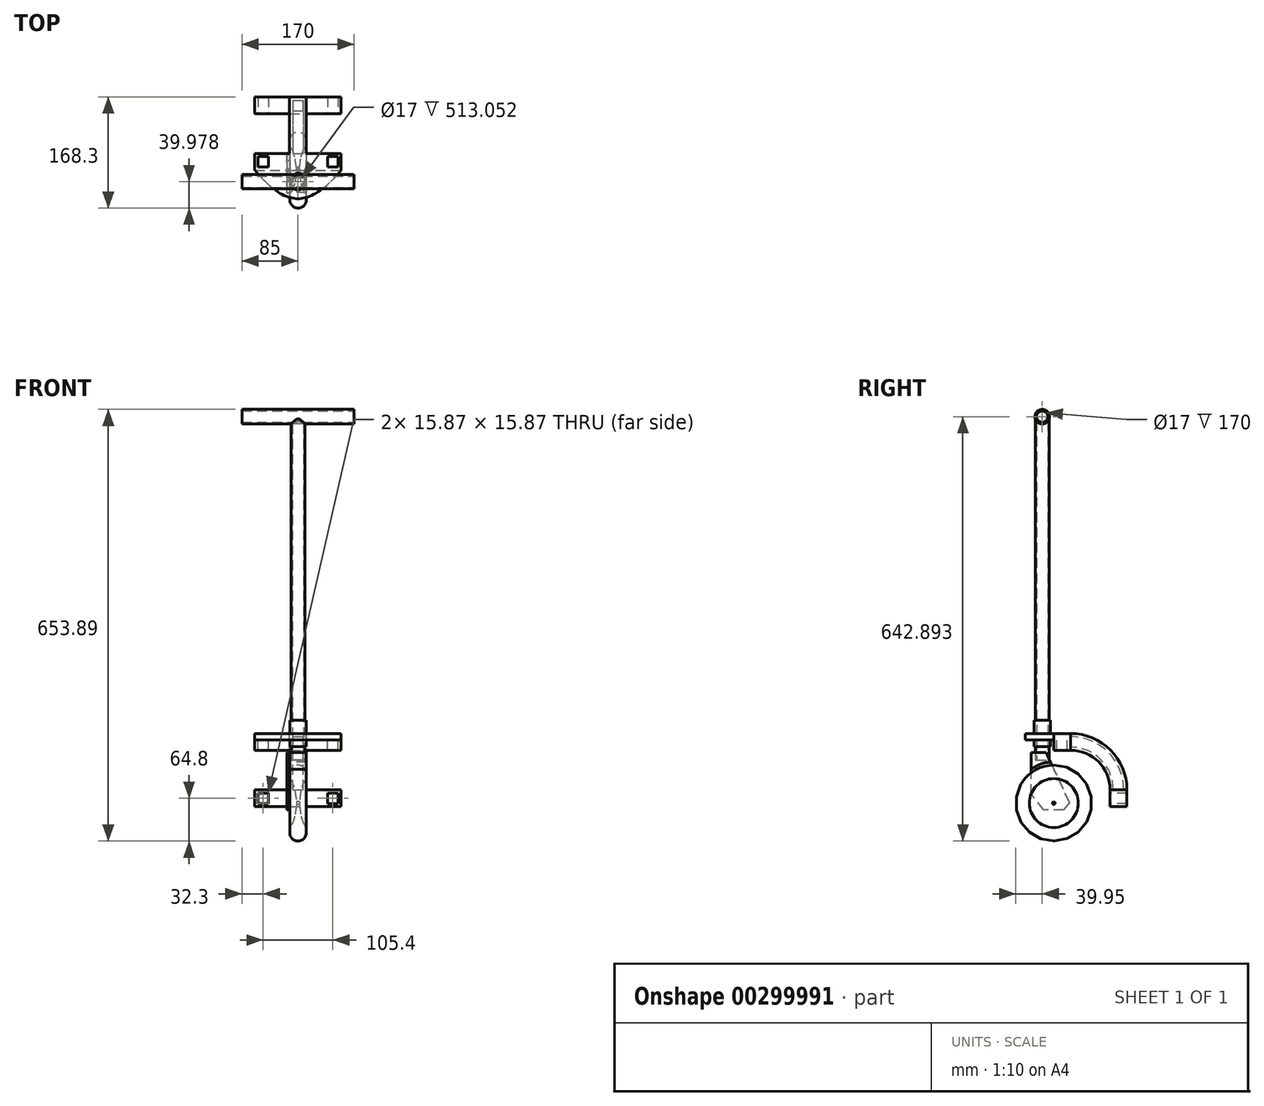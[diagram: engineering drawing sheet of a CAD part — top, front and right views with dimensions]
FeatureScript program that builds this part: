
annotation { "Feature Type Name" : "Feature", "Feature Type Description" : "" }
export const myFeature = defineFeature(function(context is Context, id is Id, definition is map)
    precondition{}
    {
        {
            var Q0;
            Q0=qCreatedBy(makeId("Top.planeOp"),FACE);
            var sketch = newSketch(context, id + "F0", { "sketchPlane" : qUnion([Q0])});
            skLineSegment(sketch, "E0.bottom", {"start": v(-12.7, 25.4) * mm, "end": v(12.7, 25.4) * mm});
            skLineSegment(sketch, "E0.top", {"start": v(-12.7, 0) * mm, "end": v(12.7, 0) * mm});
            skLineSegment(sketch, "E0.left", {"start": v(-12.7, 25.4) * mm, "end": v(-12.7, 0) * mm});
            skLineSegment(sketch, "E0.right", {"start": v(12.7, 25.4) * mm, "end": v(12.7, 0) * mm});
            skLineSegment(sketch, "E1.bottom", {"start": v(-7.94, 20.63) * mm, "end": v(7.94, 20.63) * mm});
            skLineSegment(sketch, "E1.top", {"start": v(-7.94, 4.76) * mm, "end": v(7.94, 4.76) * mm});
            skLineSegment(sketch, "E1.left", {"start": v(-7.94, 20.63) * mm, "end": v(-7.94, 4.76) * mm});
            skLineSegment(sketch, "E1.right", {"start": v(7.94, 20.63) * mm, "end": v(7.94, 4.76) * mm});
            skSolve(sketch);
        }
        {
            var Q0;
            Q0=qCreatedBy(makeId("Right.planeOp"),FACE);
            var sketch = newSketch(context, id + "F1", { "sketchPlane" : qUnion([Q0])});
            skArc(sketch, "E2", {"start": v(0, 0) * mm, "mid": v(-17.57, 42.43) * mm, "end": v(-60, 60) * mm});
            skSolve(sketch);
        }
        {
            var Q0;
            Q0 = qSketchRegion(id + "F0", true);
            var Q1;
            Q1=sQuery(id+"F1.wireOp",EDGE,"E2");
            sweep(context, id + "F2", {"profiles" : qUnion([Q0]), "path" : qUnion([Q1])});
        }
        {
            var Q0;
            Q0=makeQuery(id+"F2.opSweep","CAP_FACE",FACE,{"disambiguationData":[OSD([sQuery(id+"F0.wireOp",EDGE,"E0.bottom"),sQuery(id+"F0.wireOp",EDGE,"E0.top"),sQuery(id+"F0.wireOp",EDGE,"E0.left"),sQuery(id+"F0.wireOp",EDGE,"E0.right"),sQuery(id+"F0.wireOp",EDGE,"E1.bottom"),sQuery(id+"F0.wireOp",EDGE,"E1.top"),sQuery(id+"F0.wireOp",EDGE,"E1.left"),sQuery(id+"F0.wireOp",EDGE,"E1.right"),sQuery(id+"F1.wireOp",VERTEX,"E2.end")])],"isStart":false});
            var sketch = newSketch(context, id + "F3", { "sketchPlane" : qUnion([Q0])});
            skLineSegment(sketch, "E3.bottom", {"start": v(-12.7, 85.4) * mm, "end": v(12.7, 85.4) * mm});
            skLineSegment(sketch, "E3.top", {"start": v(-12.7, 60) * mm, "end": v(12.7, 60) * mm});
            skLineSegment(sketch, "E3.left", {"start": v(-12.7, 85.4) * mm, "end": v(-12.7, 60) * mm});
            skLineSegment(sketch, "E3.right", {"start": v(12.7, 85.4) * mm, "end": v(12.7, 60) * mm});
            skLineSegment(sketch, "E4.bottom", {"start": v(-7.94, 80.63) * mm, "end": v(7.94, 80.63) * mm});
            skLineSegment(sketch, "E4.top", {"start": v(-7.94, 64.76) * mm, "end": v(7.94, 64.76) * mm});
            skLineSegment(sketch, "E4.left", {"start": v(-7.94, 80.63) * mm, "end": v(-7.94, 64.76) * mm});
            skLineSegment(sketch, "E4.right", {"start": v(7.94, 80.63) * mm, "end": v(7.94, 64.76) * mm});
            skSolve(sketch);
        }
        {
            var Q0;
            Q0 = qSketchRegion(id + "F3", true);
            extrude(context, id + "F4", {"entities" : qUnion([Q0]), "operationType" : NewBodyOperationType.ADD, "depth" : 25.4 * mm, "offsetDistance" : 25 * mm});
        }
        {
            var Q0;
            Q0=makeQuery(id+"F2.opSweep","CAP_FACE",FACE,{"disambiguationData":[OSD([sQuery(id+"F0.wireOp",EDGE,"E0.bottom"),sQuery(id+"F0.wireOp",EDGE,"E0.top"),sQuery(id+"F0.wireOp",EDGE,"E0.left"),sQuery(id+"F0.wireOp",EDGE,"E0.right"),sQuery(id+"F0.wireOp",EDGE,"E1.bottom"),sQuery(id+"F0.wireOp",EDGE,"E1.top"),sQuery(id+"F0.wireOp",EDGE,"E1.left"),sQuery(id+"F0.wireOp",EDGE,"E1.right"),sQuery(id+"F1.wireOp",VERTEX,"E2.start")])],"isStart":true});
            var sketch = newSketch(context, id + "F5", { "sketchPlane" : qUnion([Q0])});
            skLineSegment(sketch, "E5.bottom", {"start": v(-12.7, 0) * mm, "end": v(12.7, 0) * mm});
            skLineSegment(sketch, "E5.top", {"start": v(-12.7, -25.4) * mm, "end": v(12.7, -25.4) * mm});
            skLineSegment(sketch, "E5.left", {"start": v(-12.7, 0) * mm, "end": v(-12.7, -25.4) * mm});
            skLineSegment(sketch, "E5.right", {"start": v(12.7, 0) * mm, "end": v(12.7, -25.4) * mm});
            skLineSegment(sketch, "E6.bottom", {"start": v(-7.94, -4.76) * mm, "end": v(7.94, -4.76) * mm});
            skLineSegment(sketch, "E6.top", {"start": v(-7.94, -20.63) * mm, "end": v(7.94, -20.63) * mm});
            skLineSegment(sketch, "E6.left", {"start": v(-7.94, -4.76) * mm, "end": v(-7.94, -20.63) * mm});
            skLineSegment(sketch, "E6.right", {"start": v(7.94, -4.76) * mm, "end": v(7.94, -20.63) * mm});
            skSolve(sketch);
        }
        {
            var Q0;
            Q0=makeQuery(id+"F5.imprint","IMPRINT",FACE,{"disambiguationData":[TD([[makeQuery(id+"F5.imprint","IMPRINT",EDGE,{"derivedFrom":sQuery(id+"F5.wireOp",EDGE,"E5.bottom")}),-1.0]])]});
            extrude(context, id + "F6", {"entities" : qUnion([Q0]), "operationType" : NewBodyOperationType.ADD, "depth" : 25.4 * mm, "offsetDistance" : 25 * mm});
        }
        {
            var Q0;
            Q0=qCreatedBy(makeId("Right.planeOp"),FACE);
            var sketch = newSketch(context, id + "F7", { "sketchPlane" : qUnion([Q0])});
            skLineSegment(sketch, "E7.bottom", {"start": v(0, 0) * mm, "end": v(25.4, 0) * mm});
            skLineSegment(sketch, "E7.top", {"start": v(0, -25.4) * mm, "end": v(25.4, -25.4) * mm});
            skLineSegment(sketch, "E7.left", {"start": v(0, 0) * mm, "end": v(0, -25.4) * mm});
            skLineSegment(sketch, "E7.right", {"start": v(25.4, 0) * mm, "end": v(25.4, -25.4) * mm});
            skLineSegment(sketch, "E8.bottom", {"start": v(-85.4, 60) * mm, "end": v(-60, 60) * mm});
            skLineSegment(sketch, "E8.top", {"start": v(-85.4, 85.4) * mm, "end": v(-60, 85.4) * mm});
            skLineSegment(sketch, "E8.left", {"start": v(-85.4, 60) * mm, "end": v(-85.4, 85.4) * mm});
            skLineSegment(sketch, "E8.right", {"start": v(-60, 60) * mm, "end": v(-60, 85.4) * mm});
            skSolve(sketch);
        }
        {
            var Q0;
            Q0=makeQuery(id+"F7.imprint","IMPRINT",FACE,{"disambiguationData":[TD([[makeQuery(id+"F7.imprint","IMPRINT",EDGE,{"derivedFrom":sQuery(id+"F7.wireOp",EDGE,"E7.bottom")}),-1.0]])]});
            var Q1;
            Q1=makeQuery(id+"F7.imprint","IMPRINT",FACE,{"disambiguationData":[TD([[makeQuery(id+"F7.imprint","IMPRINT",EDGE,{"derivedFrom":sQuery(id+"F7.wireOp",EDGE,"E8.bottom")}),1.0]])]});
            extrude(context, id + "F8", {"entities" : qUnion([Q0, Q1]), "operationType" : NewBodyOperationType.ADD, "endBound" : BoundingType.SYMMETRIC, "depth" : 80 * mm});
        }
        {
            var Q0;
            Q0=makeQuery(id+"F6.opExtrude","SWEPT_FACE",FACE,{"disambiguationData":[OSD([sQuery(id+"F5.wireOp",EDGE,"E5.bottom")])]});
            var sketch = newSketch(context, id + "F9", { "sketchPlane" : qUnion([Q0])});
            skLineSegment(sketch, "E9.bottom", {"start": v(40, 0) * mm, "end": v(65.4, 0) * mm});
            skLineSegment(sketch, "E9.top", {"start": v(40, -25.4) * mm, "end": v(65.4, -25.4) * mm});
            skLineSegment(sketch, "E9.left", {"start": v(40, 0) * mm, "end": v(40, -25.4) * mm});
            skLineSegment(sketch, "E9.right", {"start": v(65.4, 0) * mm, "end": v(65.4, -25.4) * mm});
            skLineSegment(sketch, "E10.bottom", {"start": v(-40, 0) * mm, "end": v(-65.4, 0) * mm});
            skLineSegment(sketch, "E10.top", {"start": v(-40, -25.4) * mm, "end": v(-65.4, -25.4) * mm});
            skLineSegment(sketch, "E10.left", {"start": v(-40, 0) * mm, "end": v(-40, -25.4) * mm});
            skLineSegment(sketch, "E10.right", {"start": v(-65.4, 0) * mm, "end": v(-65.4, -25.4) * mm});
            skLineSegment(sketch, "E11.bottom", {"start": v(-60.64, -4.76) * mm, "end": v(-44.76, -4.76) * mm});
            skLineSegment(sketch, "E11.top", {"start": v(-60.64, -20.64) * mm, "end": v(-44.76, -20.64) * mm});
            skLineSegment(sketch, "E11.left", {"start": v(-60.64, -4.76) * mm, "end": v(-60.64, -20.64) * mm});
            skLineSegment(sketch, "E11.right", {"start": v(-44.76, -4.76) * mm, "end": v(-44.76, -20.64) * mm});
            skLineSegment(sketch, "E12.bottom", {"start": v(44.76, -4.76) * mm, "end": v(60.64, -4.76) * mm});
            skLineSegment(sketch, "E12.top", {"start": v(44.76, -20.64) * mm, "end": v(60.64, -20.64) * mm});
            skLineSegment(sketch, "E12.left", {"start": v(44.76, -4.76) * mm, "end": v(44.76, -20.64) * mm});
            skLineSegment(sketch, "E12.right", {"start": v(60.64, -4.76) * mm, "end": v(60.64, -20.64) * mm});
            skSolve(sketch);
        }
        {
            var Q0;
            Q0 = qSketchRegion(id + "F9", true);
            extrude(context, id + "F10", {"entities" : qUnion([Q0]), "operationType" : NewBodyOperationType.ADD, "oppositeDirection" : true, "depth" : 25.4 * mm, "offsetDistance" : 25 * mm});
        }
        {
            var Q0;
            Q0=makeQuery(id+"F8.boolean.opBoolean","MERGE",FACE,{"derivedFrom":[makeQuery(id+"F4.opExtrude","SWEPT_FACE",FACE,{"disambiguationData":[OSD([sQuery(id+"F3.wireOp",EDGE,"E3.bottom")])]}),makeQuery(id+"F8.opExtrude","SWEPT_FACE",FACE,{"disambiguationData":[OSD([sQuery(id+"F7.wireOp",EDGE,"E8.top")])]})]});
            var sketch = newSketch(context, id + "F11", { "sketchPlane" : qUnion([Q0])});
            skLineSegment(sketch, "E13.bottom", {"start": v(-65.4, -60) * mm, "end": v(-40, -60) * mm});
            skLineSegment(sketch, "E13.top", {"start": v(-65.4, -85.4) * mm, "end": v(-40, -85.4) * mm});
            skLineSegment(sketch, "E13.left", {"start": v(-65.4, -60) * mm, "end": v(-65.4, -85.4) * mm});
            skLineSegment(sketch, "E13.right", {"start": v(-40, -60) * mm, "end": v(-40, -85.4) * mm});
            skLineSegment(sketch, "E14.bottom", {"start": v(40, -60) * mm, "end": v(65.4, -60) * mm});
            skLineSegment(sketch, "E14.top", {"start": v(40, -85.4) * mm, "end": v(65.4, -85.4) * mm});
            skLineSegment(sketch, "E14.left", {"start": v(40, -60) * mm, "end": v(40, -85.4) * mm});
            skLineSegment(sketch, "E14.right", {"start": v(65.4, -60) * mm, "end": v(65.4, -85.4) * mm});
            skLineSegment(sketch, "E15.bottom", {"start": v(-60.64, -64.76) * mm, "end": v(-44.76, -64.76) * mm});
            skLineSegment(sketch, "E15.top", {"start": v(-60.64, -80.64) * mm, "end": v(-44.76, -80.64) * mm});
            skLineSegment(sketch, "E15.left", {"start": v(-60.64, -64.76) * mm, "end": v(-60.64, -80.64) * mm});
            skLineSegment(sketch, "E15.right", {"start": v(-44.76, -64.76) * mm, "end": v(-44.76, -80.64) * mm});
            skLineSegment(sketch, "E16.bottom", {"start": v(44.76, -64.76) * mm, "end": v(60.64, -64.76) * mm});
            skLineSegment(sketch, "E16.top", {"start": v(44.76, -80.64) * mm, "end": v(60.64, -80.64) * mm});
            skLineSegment(sketch, "E16.left", {"start": v(44.76, -64.76) * mm, "end": v(44.76, -80.64) * mm});
            skLineSegment(sketch, "E16.right", {"start": v(60.64, -64.76) * mm, "end": v(60.64, -80.64) * mm});
            skSolve(sketch);
        }
        {
            var Q0;
            Q0 = qSketchRegion(id + "F11", true);
            extrude(context, id + "F12", {"entities" : qUnion([Q0]), "operationType" : NewBodyOperationType.ADD, "oppositeDirection" : true, "depth" : 25.4 * mm, "offsetDistance" : 25 * mm});
        }
        {
            var Q0;
            Q0=makeQuery(id+"F12.boolean.opBoolean","MERGE",FACE,{"derivedFrom":[makeQuery(id+"F8.boolean.opBoolean","MERGE",FACE,{"derivedFrom":[makeQuery(id+"F4.opExtrude","SWEPT_FACE",FACE,{"disambiguationData":[OSD([sQuery(id+"F3.wireOp",EDGE,"E3.bottom")])]}),makeQuery(id+"F8.opExtrude","SWEPT_FACE",FACE,{"disambiguationData":[OSD([sQuery(id+"F7.wireOp",EDGE,"E8.top")])]})]}),makeQuery(id+"F12.opExtrude","CAP_FACE",FACE,{"disambiguationData":[OSD([sQuery(id+"F11.wireOp",EDGE,"E13.bottom"),sQuery(id+"F11.wireOp",EDGE,"E13.top"),sQuery(id+"F11.wireOp",EDGE,"E13.left"),sQuery(id+"F11.wireOp",EDGE,"E13.right"),sQuery(id+"F11.wireOp",EDGE,"E15.bottom"),sQuery(id+"F11.wireOp",EDGE,"E15.top"),sQuery(id+"F11.wireOp",EDGE,"E15.left"),sQuery(id+"F11.wireOp",EDGE,"E15.right")])],"isStart":true}),makeQuery(id+"F12.opExtrude","CAP_FACE",FACE,{"disambiguationData":[OSD([sQuery(id+"F11.wireOp",EDGE,"E14.bottom"),sQuery(id+"F11.wireOp",EDGE,"E14.top"),sQuery(id+"F11.wireOp",EDGE,"E14.left"),sQuery(id+"F11.wireOp",EDGE,"E14.right"),sQuery(id+"F11.wireOp",EDGE,"E16.bottom"),sQuery(id+"F11.wireOp",EDGE,"E16.top"),sQuery(id+"F11.wireOp",EDGE,"E16.left"),sQuery(id+"F11.wireOp",EDGE,"E16.right")])],"isStart":true})]});
            var sketch = newSketch(context, id + "F13", { "sketchPlane" : qUnion([Q0])});
            skCircle(sketch, "E17", {"center": v(0, -102.92) * mm, "radius": 12.5 * mm});
            skFitSpline(sketch, "E18", {"points": [v(-65.4, -85.4) * mm, v(0, -128.66) * mm, v(65.4, -85.4) * mm], "startDerivative": vector(120, -145.97) * mm, "endDerivative": vector(120, 145.97) * mm});
            skLineSegment(sketch, "E19", {"start": v(-65.4, -85.4) * mm, "end": v(65.4, -85.4) * mm});
            skSolve(sketch);
        }
        {
            var Q0;
            Q0 = qSketchRegion(id + "F13", true);
            extrude(context, id + "F14", {"entities" : qUnion([Q0]), "operationType" : NewBodyOperationType.ADD, "oppositeDirection" : true, "depth" : 10 * mm});
        }
        {
            var Q0;
            Q0=makeQuery(id+"F14.boolean.opBoolean","MERGE",FACE,{"derivedFrom":[makeQuery(id+"F12.boolean.opBoolean","MERGE",FACE,{"derivedFrom":[makeQuery(id+"F8.boolean.opBoolean","MERGE",FACE,{"derivedFrom":[makeQuery(id+"F4.opExtrude","SWEPT_FACE",FACE,{"disambiguationData":[OSD([sQuery(id+"F3.wireOp",EDGE,"E3.bottom")])]}),makeQuery(id+"F8.opExtrude","SWEPT_FACE",FACE,{"disambiguationData":[OSD([sQuery(id+"F7.wireOp",EDGE,"E8.top")])]})]}),makeQuery(id+"F12.opExtrude","CAP_FACE",FACE,{"disambiguationData":[OSD([sQuery(id+"F11.wireOp",EDGE,"E13.bottom"),sQuery(id+"F11.wireOp",EDGE,"E13.top"),sQuery(id+"F11.wireOp",EDGE,"E13.left"),sQuery(id+"F11.wireOp",EDGE,"E13.right"),sQuery(id+"F11.wireOp",EDGE,"E15.bottom"),sQuery(id+"F11.wireOp",EDGE,"E15.top"),sQuery(id+"F11.wireOp",EDGE,"E15.left"),sQuery(id+"F11.wireOp",EDGE,"E15.right")])],"isStart":true}),makeQuery(id+"F12.opExtrude","CAP_FACE",FACE,{"disambiguationData":[OSD([sQuery(id+"F11.wireOp",EDGE,"E14.bottom"),sQuery(id+"F11.wireOp",EDGE,"E14.top"),sQuery(id+"F11.wireOp",EDGE,"E14.left"),sQuery(id+"F11.wireOp",EDGE,"E14.right"),sQuery(id+"F11.wireOp",EDGE,"E16.bottom"),sQuery(id+"F11.wireOp",EDGE,"E16.top"),sQuery(id+"F11.wireOp",EDGE,"E16.left"),sQuery(id+"F11.wireOp",EDGE,"E16.right")])],"isStart":true})]}),makeQuery(id+"F14.opExtrude","CAP_FACE",FACE,{"disambiguationData":[OSD([sQuery(id+"F13.wireOp",EDGE,"E17"),sQuery(id+"F13.wireOp",EDGE,"E18"),sQuery(id+"F13.wireOp",EDGE,"E19")])],"isStart":true})]});
            var sketch = newSketch(context, id + "F15", { "sketchPlane" : qUnion([Q0])});
            skCircle(sketch, "E20", {"center": v(0, -102.92) * mm, "radius": 12.5 * mm});
            skCircle(sketch, "E21", {"center": v(0, -102.92) * mm, "radius": 10.5 * mm});
            skSolve(sketch);
        }
        {
            var Q0;
            Q0=makeQuery(id+"F15.imprint","IMPRINT",FACE,{"disambiguationData":[TD([[makeQuery(id+"F15.imprint","IMPRINT",EDGE,{"derivedFrom":sQuery(id+"F15.wireOp",EDGE,"E20")}),1.0]])]});
            extrude(context, id + "F16", {"entities" : qUnion([Q0]), "operationType" : NewBodyOperationType.ADD, "endBound" : BoundingType.SYMMETRIC, "depth" : 40 * mm});
        }
        {
            var Q0;
            Q0=makeQuery(id+"F16.opExtrude","CAP_FACE",FACE,{"disambiguationData":[OSD([sQuery(id+"F15.wireOp",EDGE,"E20"),sQuery(id+"F15.wireOp",EDGE,"E21")])],"isStart":false});
            var sketch = newSketch(context, id + "F17", { "sketchPlane" : qUnion([Q0])});
            skCircle(sketch, "E22", {"center": v(0, -102.92) * mm, "radius": 10.5 * mm});
            skCircle(sketch, "E23", {"center": v(0, -102.92) * mm, "radius": 8.5 * mm});
            skSolve(sketch);
        }
        {
            var Q0;
            Q0 = qSketchRegion(id + "F17", true);
            extrude(context, id + "F18", {"entities" : qUnion([Q0]), "operationType" : NewBodyOperationType.ADD, "endBound" : BoundingType.SYMMETRIC, "depth" : 120 * mm});
        }
        {
            var Q0;
            Q0=makeQuery(id+"F12.boolean.opBoolean","MERGE",FACE,{"derivedFrom":[makeQuery(id+"F8.boolean.opBoolean","MERGE",FACE,{"derivedFrom":[makeQuery(id+"F4.opExtrude","CAP_FACE",FACE,{"disambiguationData":[OSD([sQuery(id+"F3.wireOp",EDGE,"E3.bottom"),sQuery(id+"F3.wireOp",EDGE,"E3.top"),sQuery(id+"F3.wireOp",EDGE,"E3.left"),sQuery(id+"F3.wireOp",EDGE,"E3.right"),sQuery(id+"F3.wireOp",EDGE,"E4.bottom"),sQuery(id+"F3.wireOp",EDGE,"E4.top"),sQuery(id+"F3.wireOp",EDGE,"E4.left"),sQuery(id+"F3.wireOp",EDGE,"E4.right")])],"isStart":false}),makeQuery(id+"F8.opExtrude","SWEPT_FACE",FACE,{"disambiguationData":[OSD([sQuery(id+"F7.wireOp",EDGE,"E8.left")])]})]}),makeQuery(id+"F12.opExtrude","SWEPT_FACE",FACE,{"disambiguationData":[OSD([sQuery(id+"F11.wireOp",EDGE,"E13.top")])]}),makeQuery(id+"F12.opExtrude","SWEPT_FACE",FACE,{"disambiguationData":[OSD([sQuery(id+"F11.wireOp",EDGE,"E14.top")])]})]});
            var sketch = newSketch(context, id + "F19", { "sketchPlane" : qUnion([Q0])});
            skLineSegment(sketch, "E24", {"start": v(-42.08, 0) * mm, "end": v(44.88, 0) * mm});
            skLineSegment(sketch, "E25", {"start": v(-42.08, 0) * mm, "end": v(-42.08, -20) * mm});
            skLineSegment(sketch, "E26", {"start": v(-42.08, -20) * mm, "end": v(44.9, -20) * mm});
            skArc(sketch, "E27", {"start": v(12.5, 25) * mm, "mid": v(0, 37.5) * mm, "end": v(-12.5, 25) * mm});
            skLineSegment(sketch, "E28", {"start": v(12.5, 25) * mm, "end": v(12.5, 17) * mm});
            skLineSegment(sketch, "E29", {"start": v(-12.5, 25) * mm, "end": v(-12.5, 17) * mm});
            skLineSegment(sketch, "E30", {"start": v(-2, -18) * mm, "end": v(2, -18) * mm});
            skFitSpline(sketch, "E31", {"points": [v(12.5, 17) * mm, v(2, -18) * mm], "startDerivative": vector(-27.06, -33.3) * mm, "endDerivative": vector(-5.87, -32.43) * mm});
            skFitSpline(sketch, "E32", {"points": [v(-12.5, 17) * mm, v(-2, -18) * mm], "startDerivative": vector(24.33, -32.22) * mm, "endDerivative": vector(6.89, -31.88) * mm});
            skSolve(sketch);
        }
        {
            var Q0;
            Q0 = qSketchRegion(id + "F19", true);
            var Q1;
            Q1=sQuery(id+"F19.wireOp",EDGE,"E26");
            revolve(context, id + "F20", {"operationType" : NewBodyOperationType.ADD, "entities" : qUnion([Q0]), "axis" : qUnion([Q1]), "revolveType" : RevolveType.FULL});
        }
        {
            var Q0;
            Q0=makeQuery(id+"F18.opExtrude","CAP_FACE",FACE,{"disambiguationData":[OSD([sQuery(id+"F17.wireOp",EDGE,"E22"),sQuery(id+"F17.wireOp",EDGE,"E23")])],"isStart":false});
            var sketch = newSketch(context, id + "F21", { "sketchPlane" : qUnion([Q0])});
            skCircle(sketch, "E33", {"center": v(0, -102.92) * mm, "radius": 8.5 * mm});
            skCircle(sketch, "E34", {"center": v(0, -102.92) * mm, "radius": 10.5 * mm});
            skSolve(sketch);
        }
        {
            var Q0;
            Q0 = qSketchRegion(id + "F21", true);
            extrude(context, id + "F22", {"entities" : qUnion([Q0]), "operationType" : NewBodyOperationType.ADD, "depth" : 400 * mm});
        }
        {
            var Q0;
            Q0=qCreatedBy(makeId("Right.planeOp"),FACE);
            var sketch = newSketch(context, id + "F23", { "sketchPlane" : qUnion([Q0])});
            skCircle(sketch, "E35", {"center": v(-102.95, 565.4) * mm, "radius": 11 * mm});
            skLineSegment(sketch, "E36", {"start": v(-113.45, 565.4) * mm, "end": v(-102.95, 565.4) * mm});
            skSolve(sketch);
        }
        {
            var Q0;
            Q0 = qSketchRegion(id + "F23", true);
            extrude(context, id + "F24", {"entities" : qUnion([Q0]), "operationType" : NewBodyOperationType.ADD, "endBound" : BoundingType.SYMMETRIC, "depth" : 170 * mm});
        }
        {
            var Q0;
            Q0=makeQuery(id+"F20.opRevolve","SWEPT_FACE",FACE,{"disambiguationData":[OSD([sQuery(id+"F19.wireOp",EDGE,"E29")])]});
            var sketch = newSketch(context, id + "F25", { "sketchPlane" : qUnion([Q0])});
            skLineSegment(sketch, "E37", {"start": v(70.5, -30.66) * mm, "end": v(100.44, -30.66) * mm});
            skLineSegment(sketch, "E38", {"start": v(100.44, -30.66) * mm, "end": v(119.8, -6.38) * mm});
            skLineSegment(sketch, "E39", {"start": v(119.8, -6.38) * mm, "end": v(119.36, 56.64) * mm});
            skLineSegment(sketch, "E40", {"start": v(119.36, 56.64) * mm, "end": v(97.1, 56.64) * mm});
            skLineSegment(sketch, "E41", {"start": v(97.1, 56.64) * mm, "end": v(61.76, -19.91) * mm});
            skLineSegment(sketch, "E42", {"start": v(61.76, -19.91) * mm, "end": v(70.5, -30.66) * mm});
            skCircle(sketch, "E43", {"center": v(85.4, -20) * mm, "radius": 2 * mm});
            skSolve(sketch);
        }
        {
            var Q0;
            Q0 = qSketchRegion(id + "F25", true);
            extrude(context, id + "F26", {"entities" : qUnion([Q0]), "depth" : 4 * mm});
        }
        {
            var Q0;
            Q0=makeQuery(id+"F24.opExtrude","CAP_FACE",FACE,{"disambiguationData":[OSD([sQuery(id+"F23.wireOp",EDGE,"E35")])],"isStart":false});
            var sketch = newSketch(context, id + "F27", { "sketchPlane" : qUnion([Q0])});
            skCircle(sketch, "E44", {"center": v(-102.95, 565.4) * mm, "radius": 8.5 * mm});
            skSolve(sketch);
        }
        {
            var Q0;
            Q0 = qSketchRegion(id + "F27", true);
            extrude(context, id + "F28", {"entities" : qUnion([Q0]), "operationType" : NewBodyOperationType.REMOVE, "oppositeDirection" : true, "depth" : 175.6 * mm});
        }
        {
            var Q0;
            {var subQ0=sQuery(id+"F25.wireOp",EDGE,"E40");var subQ1=sQuery(id+"F25.wireOp",EDGE,"E39");var subQ2=sQuery(id+"F25.wireOp",EDGE,"E41");Q0=makeQuery(id+"FLBI3LbdFqLThpN_3.opBoolean","SPLIT",FACE,{"disambiguationData":[TD([makeQuery(id+"F20.opRevolve","SWEPT_FACE",FACE,{"disambiguationData":[OSD([sQuery(id+"F19.wireOp",EDGE,"E27")])]})])],"derivedFrom":makeQuery(id+"F26.opExtrude","CAP_FACE",FACE,{"disambiguationData":[OSD([sQuery(id+"F25.wireOp",EDGE,"E37"),sQuery(id+"F25.wireOp",EDGE,"E38"),subQ1,subQ0,subQ2,sQuery(id+"F25.wireOp",EDGE,"E42"),sQuery(id+"F25.wireOp",EDGE,"E43")])],"isStart":true})});}
            var sketch = newSketch(context, id + "F29", { "sketchPlane" : qUnion([Q0])});
            skLineSegment(sketch, "E45", {"start": v(-119.36, 56.64) * mm, "end": v(-97.1, 56.64) * mm});
            skLineSegment(sketch, "E46", {"start": v(-97.1, 56.64) * mm, "end": v(-79.43, 18.36) * mm});
            skPoint(sketch, "E47.endSnap0", {"position": v(-119.58, 25.13) * mm});
            skLineSegment(sketch, "E48", {"start": v(-119.58, 25.13) * mm, "end": v(-119.36, 56.64) * mm});
            skFitSpline(sketch, "E49", {"points": [v(-119.54, 31.31) * mm, v(-90.3, 41.93) * mm], "startDerivative": vector(29.21, 18.18) * mm, "endDerivative": vector(38.66, 1.42) * mm});
            skSolve(sketch);
        }
        {
            var Q0;
            Q0 = qSketchRegion(id + "F29", true);
            extrude(context, id + "F30", {"entities" : qUnion([Q0]), "depth" : 25 * mm});
        }
    });
